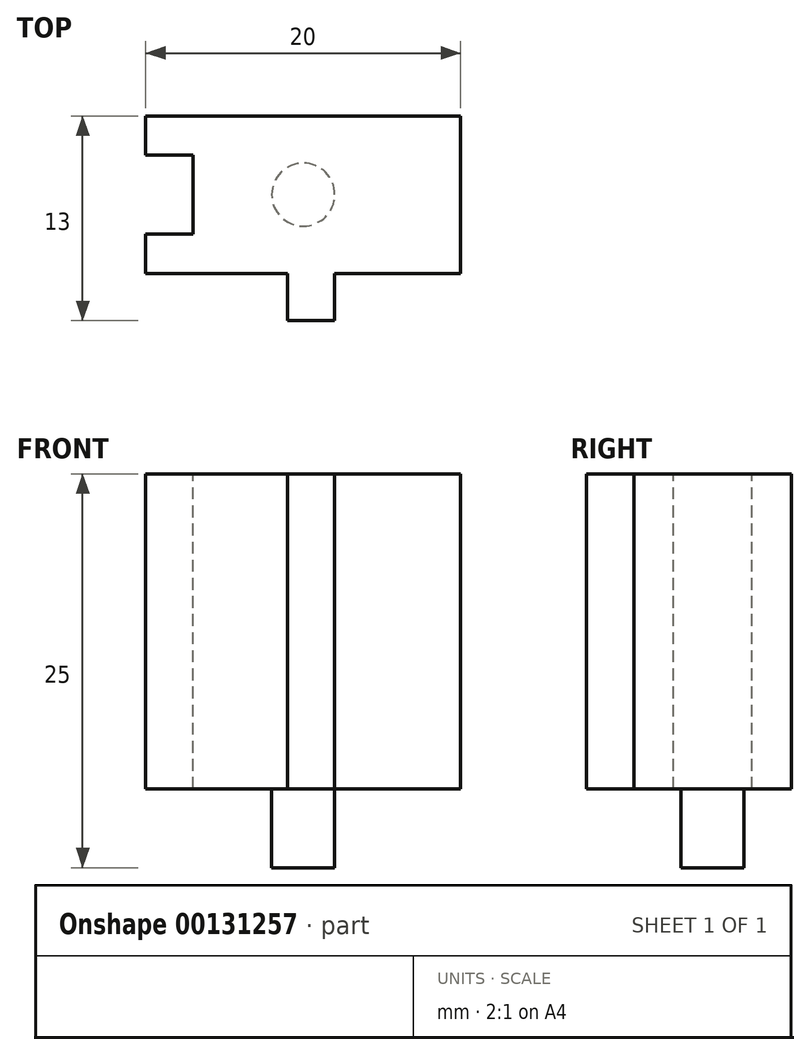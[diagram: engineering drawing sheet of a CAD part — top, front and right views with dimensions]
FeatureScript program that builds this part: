
annotation { "Feature Type Name" : "Feature", "Feature Type Description" : "" }
export const myFeature = defineFeature(function(context is Context, id is Id, definition is map)
    precondition{}
    {
        {
            var Q0;
            Q0=qCreatedBy(makeId("Top.planeOp"),FACE);
            var sketch = newSketch(context, id + "F0", { "sketchPlane" : qUnion([Q0])});
            skLineSegment(sketch, "E0", {"start": v(0, 0) * mm, "end": v(20, 0) * mm});
            skLineSegment(sketch, "E1", {"start": v(20, 0) * mm, "end": v(20, 10) * mm});
            skLineSegment(sketch, "E2", {"start": v(20, 10) * mm, "end": v(0, 10) * mm});
            skLineSegment(sketch, "E3", {"start": v(0, 10) * mm, "end": v(0, 0) * mm});
            skSolve(sketch);
        }
        {
            var Q0;
            Q0=makeQuery(id+"F0.imprint","IMPRINT",FACE,{"disambiguationData":[TD([[makeQuery(id+"F0.imprint","IMPRINT",EDGE,{"derivedFrom":sQuery(id+"F0.wireOp",EDGE,"E0")}),1.0]])]});
            extrude(context, id + "F1", {"entities" : qUnion([Q0]), "depth" : 20 * mm});
        }
        {
            var Q0;
            Q0=makeQuery(id+"F1.opExtrude","CAP_FACE",FACE,{"disambiguationData":[OSD([sQuery(id+"F0.wireOp",EDGE,"E0"),sQuery(id+"F0.wireOp",EDGE,"E1"),sQuery(id+"F0.wireOp",EDGE,"E2"),sQuery(id+"F0.wireOp",EDGE,"E3")])],"isStart":false});
            var sketch = newSketch(context, id + "F2", { "sketchPlane" : qUnion([Q0])});
            skLineSegment(sketch, "E4", {"start": v(0, 5) * mm, "end": v(20, 5) * mm, "construction": true});
            skLineSegment(sketch, "E5", {"start": v(10, 10) * mm, "end": v(10, 0) * mm, "construction": true});
            skLineSegment(sketch, "E6", {"start": v(0, 7.5) * mm, "end": v(3, 7.5) * mm});
            skLineSegment(sketch, "E7", {"start": v(3, 7.5) * mm, "end": v(3, 2.5) * mm});
            skLineSegment(sketch, "E8", {"start": v(3, 2.5) * mm, "end": v(0, 2.5) * mm});
            skLineSegment(sketch, "E9", {"start": v(0, 2.5) * mm, "end": v(0, 7.5) * mm});
            skLineSegment(sketch, "E10", {"start": v(9, 0) * mm, "end": v(9, -3) * mm});
            skLineSegment(sketch, "E11", {"start": v(9, -3) * mm, "end": v(12, -3) * mm});
            skLineSegment(sketch, "E12", {"start": v(12, -3) * mm, "end": v(12, 0) * mm});
            skLineSegment(sketch, "E13", {"start": v(12, 0) * mm, "end": v(9, 0) * mm});
            skSolve(sketch);
        }
        {
            var Q0;
            {var subQ0=sQuery(id+"F0.wireOp",EDGE,"E3");var subQ1=sQuery(id+"F0.wireOp",EDGE,"E2");var subQ2=sQuery(id+"F0.wireOp",EDGE,"E1");var subQ3=sQuery(id+"F0.wireOp",EDGE,"E0");Q0=makeQuery(id+"FFcaGPm5NktH2jQ_1.boolean.opBoolean","MERGE",FACE,{"derivedFrom":[makeQuery(id+"F1.opExtrude","CAP_FACE",FACE,{"disambiguationData":[OSD([subQ3,subQ2,subQ1,subQ0])],"isStart":true}),makeQuery(id+"FFcaGPm5NktH2jQ_1.opExtrude","CAP_FACE",FACE,{"disambiguationData":[OSD([subQ3,subQ2,subQ1,subQ0])],"isStart":false})]});}
            var sketch = newSketch(context, id + "F3", { "sketchPlane" : qUnion([Q0])});
            skLineSegment(sketch, "E14", {"start": v(10, -10) * mm, "end": v(10, 0) * mm, "construction": true});
            skCircle(sketch, "E15", {"center": v(10, -5) * mm, "radius": 2 * mm});
            skLineSegment(sketch, "E16.0", {"start": v(0, -5) * mm, "end": v(20, -5) * mm, "construction": true});
            skSolve(sketch);
        }
        {
            var Q0;
            Q0 = qSketchRegion(id + "F3", true);
            extrude(context, id + "F4", {"entities" : qUnion([Q0]), "operationType" : NewBodyOperationType.ADD, "depth" : 5 * mm});
        }
        {
            var Q0;
            Q0 = qSketchRegion(id + "F3", true);
            extrude(context, id + "F5", {"entities" : qUnion([Q0]), "operationType" : NewBodyOperationType.ADD, "depth" : 5 * mm});
        }
        {
            var Q0;
            Q0=makeQuery(id+"F2.imprint","IMPRINT",FACE,{"disambiguationData":[TD([[makeQuery(id+"F2.imprint","IMPRINT",EDGE,{"derivedFrom":sQuery(id+"F2.wireOp",EDGE,"E6")}),-1.0]])]});
            var Q1;
            {var subQ0=sQuery(id+"F0.wireOp",EDGE,"E3");var subQ1=sQuery(id+"F0.wireOp",EDGE,"E2");var subQ2=sQuery(id+"F0.wireOp",EDGE,"E1");var subQ3=sQuery(id+"F0.wireOp",EDGE,"E0");Q1=makeQuery(id+"Fv3wjdZQL8C9d7z_1.boolean.opBoolean","MERGE",FACE,{"derivedFrom":[makeQuery(id+"F1.opExtrude","CAP_FACE",FACE,{"disambiguationData":[OSD([subQ3,subQ2,subQ1,subQ0])],"isStart":true}),makeQuery(id+"Fv3wjdZQL8C9d7z_1.opExtrude","CAP_FACE",FACE,{"disambiguationData":[OSD([subQ3,subQ2,subQ1,subQ0])],"isStart":false})]});}
            extrude(context, id + "F6", {"entities" : qUnion([Q0]), "operationType" : NewBodyOperationType.REMOVE, "endBound" : BoundingType.UP_TO_SURFACE, "oppositeDirection" : true, "endBoundEntityFace" : qUnion([Q1]), "depth" : 25 * mm});
        }
        {
            var Q0;
            Q0 = qSketchRegion(id + "F2", true);
            var Q1;
            Q1=qCreatedBy(makeId("Top.planeOp"),FACE);
            extrude(context, id + "F7", {"entities" : qUnion([Q0]), "operationType" : NewBodyOperationType.ADD, "endBound" : BoundingType.UP_TO_SURFACE, "oppositeDirection" : true, "endBoundEntityFace" : qUnion([Q1]), "depth" : 25 * mm});
        }
        {
            var Q0;
            Q0=makeQuery(id+"F2.imprint","IMPRINT",FACE,{"disambiguationData":[TD([[makeQuery(id+"F2.imprint","IMPRINT",EDGE,{"derivedFrom":sQuery(id+"F2.wireOp",EDGE,"E6")}),-1.0]])]});
            var Q1;
            {var subQ0=dummyQuery(id+"Top.planeOp",FACE);Q1=makeQuery(id+"F7.boolean.opBoolean","MERGE",FACE,{"derivedFrom":[makeQuery(id+"F1.opExtrude","CAP_FACE",FACE,{"disambiguationData":[OSD([sQuery(id+"F0.wireOp",EDGE,"E0"),sQuery(id+"F0.wireOp",EDGE,"E1"),sQuery(id+"F0.wireOp",EDGE,"E2"),sQuery(id+"F0.wireOp",EDGE,"E3")])],"isStart":true}),makeQuery(id+"F7.opExtrude","CAP_FACE",FACE,{"disambiguationData":[OSD([subQ0]),ownerDisambiguation([makeQuery(id+"F7.opExtrude","SWEPT_BODY",BODY,{"disambiguationData":[OSD([sQuery(id+"F2.wireOp",EDGE,"E6"),sQuery(id+"F2.wireOp",EDGE,"E7"),sQuery(id+"F2.wireOp",EDGE,"E8"),sQuery(id+"F2.wireOp",EDGE,"E9")])]})])],"isStart":false}),makeQuery(id+"F7.opExtrude","CAP_FACE",FACE,{"disambiguationData":[OSD([subQ0]),ownerDisambiguation([makeQuery(id+"F7.opExtrude","SWEPT_BODY",BODY,{"disambiguationData":[OSD([sQuery(id+"F2.wireOp",EDGE,"E10"),sQuery(id+"F2.wireOp",EDGE,"E11"),sQuery(id+"F2.wireOp",EDGE,"E12"),sQuery(id+"F2.wireOp",EDGE,"E13")])]})])],"isStart":false})]});}
            extrude(context, id + "F8", {"entities" : qUnion([Q0]), "operationType" : NewBodyOperationType.REMOVE, "endBound" : BoundingType.UP_TO_SURFACE, "oppositeDirection" : true, "endBoundEntityFace" : qUnion([Q1]), "depth" : 25 * mm});
        }
    });
